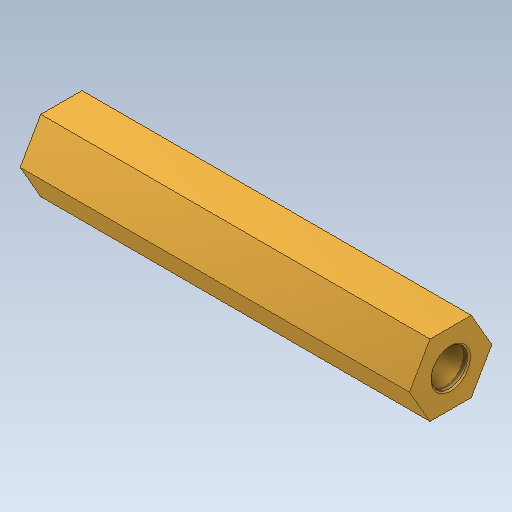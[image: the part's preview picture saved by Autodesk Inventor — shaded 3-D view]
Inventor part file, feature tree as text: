
AUTODESK INVENTOR PART (.ipt)
format: ipt  version: 2021 (Build 250183000, 183)  size: 123,392 bytes
history: native  units: mm
features: other x5, thread x4, chamfer x2, revolve x1
ambient origin geometry x6: Origin, XZ Plane, XY Plane, X Axis, Y Axis, Z Axis
bodies: Solid1 (feature_tree)
feature tree (12):
  revolve  "Revolution1"  [1 undecoded]
  other  "N-Side1"
  thread  "Thread4"  [1 undecoded]
  thread  "Thread2"  [1 undecoded]
  other  "Start Plane"
  other  "Origin point"
  other  "Main Sketch"
  other  "iFeature1:1"
  thread  "Thread1"  [1 undecoded]
  chamfer  "Chamfer1"  [1 undecoded]
  thread  "Thread3"  [1 undecoded]
  chamfer  "Chamfer2"  Distance=0.09mm Angle=45.0deg
note: 6 required parameter values undecoded (feature->parameter linkage not recoverable at this tier; creation-order binding heuristic only, values carry confidence <= 0.55)